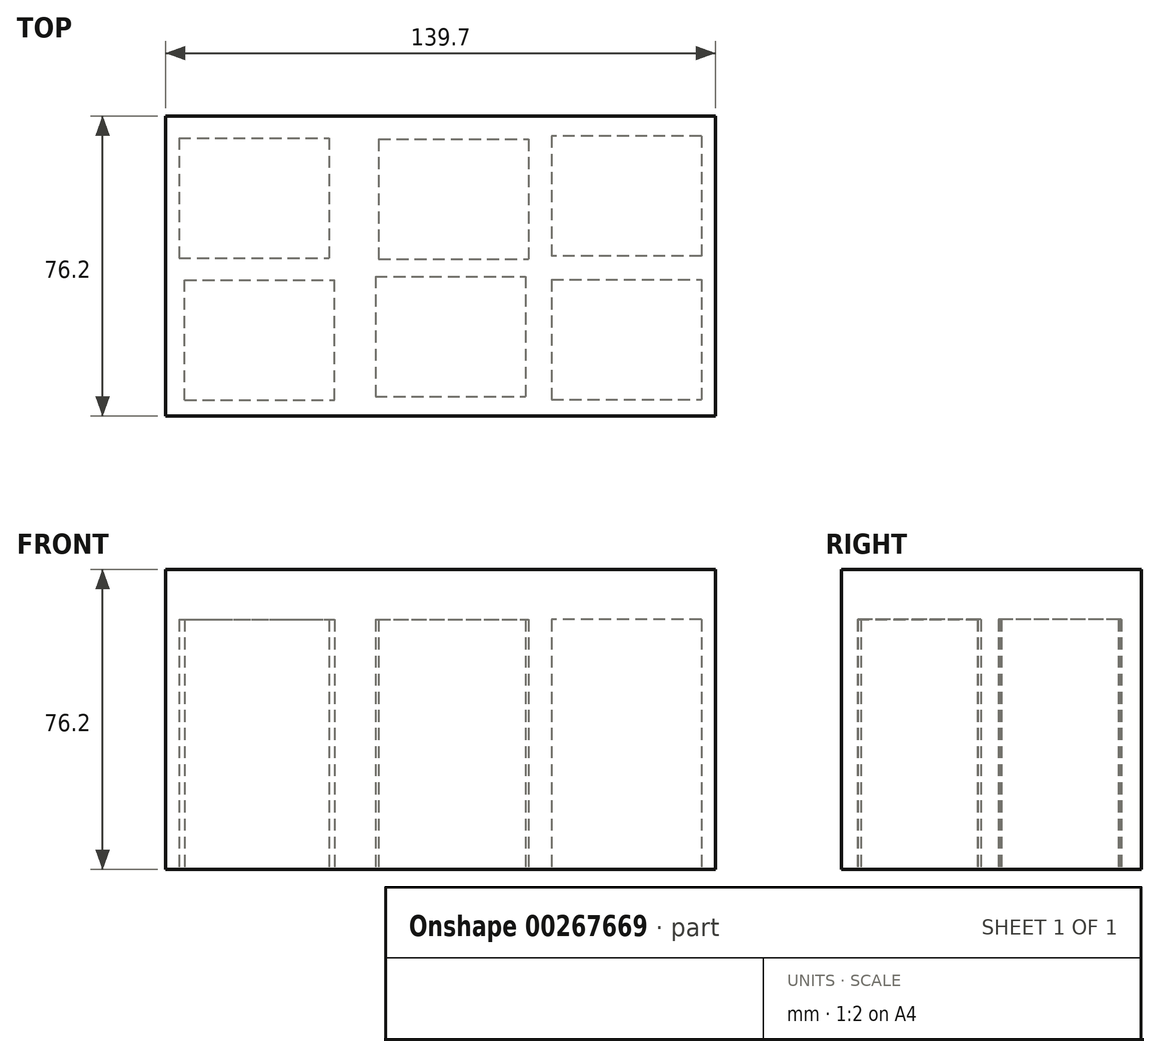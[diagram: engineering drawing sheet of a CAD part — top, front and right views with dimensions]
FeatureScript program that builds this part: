
annotation { "Feature Type Name" : "Feature", "Feature Type Description" : "" }
export const myFeature = defineFeature(function(context is Context, id is Id, definition is map)
    precondition{}
    {
        {
            var Q0;
            Q0=qCreatedBy(makeId("Top.planeOp"),FACE);
            var sketch = newSketch(context, id + "F0", { "sketchPlane" : qUnion([Q0])});
            skLineSegment(sketch, "E0.bottom", {"start": v(-69.85, -38.1) * mm, "end": v(69.85, -38.1) * mm});
            skLineSegment(sketch, "E0.top", {"start": v(-69.85, 38.1) * mm, "end": v(69.85, 38.1) * mm});
            skLineSegment(sketch, "E0.left", {"start": v(-69.85, -38.1) * mm, "end": v(-69.85, 38.1) * mm});
            skLineSegment(sketch, "E0.right", {"start": v(69.85, -38.1) * mm, "end": v(69.85, 38.1) * mm});
            skPoint(sketch, "E0.middle", {"position": v(0, 0) * mm});
            skLineSegment(sketch, "E1.bottom", {"start": v(-66.44, 32.56) * mm, "end": v(-28.34, 32.56) * mm});
            skLineSegment(sketch, "E1.top", {"start": v(-66.44, 2.08) * mm, "end": v(-28.34, 2.08) * mm});
            skLineSegment(sketch, "E1.left", {"start": v(-66.44, 32.56) * mm, "end": v(-66.44, 2.08) * mm});
            skLineSegment(sketch, "E1.right", {"start": v(-28.34, 32.56) * mm, "end": v(-28.34, 2.08) * mm});
            skLineSegment(sketch, "E2.bottom", {"start": v(-65.03, -34.1) * mm, "end": v(-26.93, -34.1) * mm});
            skLineSegment(sketch, "E2.top", {"start": v(-65.03, -3.61) * mm, "end": v(-26.93, -3.61) * mm});
            skLineSegment(sketch, "E2.left", {"start": v(-65.03, -34.1) * mm, "end": v(-65.03, -3.61) * mm});
            skLineSegment(sketch, "E2.right", {"start": v(-26.93, -34.1) * mm, "end": v(-26.93, -3.61) * mm});
            skLineSegment(sketch, "E3.bottom", {"start": v(-15.77, 32.25) * mm, "end": v(22.33, 32.25) * mm});
            skLineSegment(sketch, "E3.top", {"start": v(-15.77, 1.77) * mm, "end": v(22.33, 1.77) * mm});
            skLineSegment(sketch, "E3.left", {"start": v(-15.77, 32.25) * mm, "end": v(-15.77, 1.77) * mm});
            skLineSegment(sketch, "E3.right", {"start": v(22.33, 32.25) * mm, "end": v(22.33, 1.77) * mm});
            skLineSegment(sketch, "E4.bottom", {"start": v(66.28, 33.04) * mm, "end": v(28.18, 33.04) * mm});
            skLineSegment(sketch, "E4.top", {"start": v(66.28, 2.56) * mm, "end": v(28.18, 2.56) * mm});
            skLineSegment(sketch, "E4.left", {"start": v(66.28, 33.04) * mm, "end": v(66.28, 2.56) * mm});
            skLineSegment(sketch, "E4.right", {"start": v(28.18, 33.04) * mm, "end": v(28.18, 2.56) * mm});
            skLineSegment(sketch, "E5.bottom", {"start": v(-16.55, -2.63) * mm, "end": v(21.55, -2.63) * mm});
            skLineSegment(sketch, "E5.top", {"start": v(-16.55, -33.1) * mm, "end": v(21.55, -33.1) * mm});
            skLineSegment(sketch, "E5.left", {"start": v(-16.55, -2.63) * mm, "end": v(-16.55, -33.1) * mm});
            skLineSegment(sketch, "E5.right", {"start": v(21.55, -2.63) * mm, "end": v(21.55, -33.1) * mm});
            skLineSegment(sketch, "E6.bottom", {"start": v(28.18, -3.42) * mm, "end": v(66.28, -3.42) * mm});
            skLineSegment(sketch, "E6.top", {"start": v(28.18, -33.9) * mm, "end": v(66.28, -33.9) * mm});
            skLineSegment(sketch, "E6.left", {"start": v(28.18, -3.42) * mm, "end": v(28.18, -33.9) * mm});
            skLineSegment(sketch, "E6.right", {"start": v(66.28, -3.42) * mm, "end": v(66.28, -33.9) * mm});
            skSolve(sketch);
        }
        {
            var Q0;
            Q0=makeQuery(id+"F0.imprint","IMPRINT",FACE,{"disambiguationData":[TD([[makeQuery(id+"F0.imprint","IMPRINT",EDGE,{"derivedFrom":sQuery(id+"F0.wireOp",EDGE,"E0.bottom")}),1.0]])]});
            var Q1;
            Q1=makeQuery(id+"F0.imprint","IMPRINT",FACE,{"disambiguationData":[TD([[makeQuery(id+"F0.imprint","IMPRINT",EDGE,{"derivedFrom":sQuery(id+"F0.wireOp",EDGE,"E1.bottom")}),-1.0]])]});
            var Q2;
            Q2=makeQuery(id+"F0.imprint","IMPRINT",FACE,{"disambiguationData":[TD([[makeQuery(id+"F0.imprint","IMPRINT",EDGE,{"derivedFrom":sQuery(id+"F0.wireOp",EDGE,"E3.bottom")}),-1.0]])]});
            var Q3;
            Q3=makeQuery(id+"F0.imprint","IMPRINT",FACE,{"disambiguationData":[TD([[makeQuery(id+"F0.imprint","IMPRINT",EDGE,{"derivedFrom":sQuery(id+"F0.wireOp",EDGE,"E4.bottom")}),1.0]])]});
            var Q4;
            Q4=makeQuery(id+"F0.imprint","IMPRINT",FACE,{"disambiguationData":[TD([[makeQuery(id+"F0.imprint","IMPRINT",EDGE,{"derivedFrom":sQuery(id+"F0.wireOp",EDGE,"E6.bottom")}),-1.0]])]});
            var Q5;
            Q5=makeQuery(id+"F0.imprint","IMPRINT",FACE,{"disambiguationData":[TD([[makeQuery(id+"F0.imprint","IMPRINT",EDGE,{"derivedFrom":sQuery(id+"F0.wireOp",EDGE,"E5.bottom")}),-1.0]])]});
            var Q6;
            Q6=makeQuery(id+"F0.imprint","IMPRINT",FACE,{"disambiguationData":[TD([[makeQuery(id+"F0.imprint","IMPRINT",EDGE,{"derivedFrom":sQuery(id+"F0.wireOp",EDGE,"E2.bottom")}),1.0]])]});
            extrude(context, id + "F1", {"entities" : qUnion([Q0, Q1, Q2, Q3, Q4, Q5, Q6]), "depth" : 76.2 * mm});
        }
        {
            var Q0;
            Q0=makeQuery(id+"F0.imprint","IMPRINT",FACE,{"disambiguationData":[TD([[makeQuery(id+"F0.imprint","IMPRINT",EDGE,{"derivedFrom":sQuery(id+"F0.wireOp",EDGE,"E1.bottom")}),-1.0]])]});
            var Q1;
            Q1=makeQuery(id+"F0.imprint","IMPRINT",FACE,{"disambiguationData":[TD([[makeQuery(id+"F0.imprint","IMPRINT",EDGE,{"derivedFrom":sQuery(id+"F0.wireOp",EDGE,"E3.bottom")}),-1.0]])]});
            var Q2;
            Q2=makeQuery(id+"F0.imprint","IMPRINT",FACE,{"disambiguationData":[TD([[makeQuery(id+"F0.imprint","IMPRINT",EDGE,{"derivedFrom":sQuery(id+"F0.wireOp",EDGE,"E4.bottom")}),1.0]])]});
            var Q3;
            Q3=makeQuery(id+"F0.imprint","IMPRINT",FACE,{"disambiguationData":[TD([[makeQuery(id+"F0.imprint","IMPRINT",EDGE,{"derivedFrom":sQuery(id+"F0.wireOp",EDGE,"E6.bottom")}),-1.0]])]});
            var Q4;
            Q4=makeQuery(id+"F0.imprint","IMPRINT",FACE,{"disambiguationData":[TD([[makeQuery(id+"F0.imprint","IMPRINT",EDGE,{"derivedFrom":sQuery(id+"F0.wireOp",EDGE,"E5.bottom")}),-1.0]])]});
            var Q5;
            Q5=makeQuery(id+"F0.imprint","IMPRINT",FACE,{"disambiguationData":[TD([[makeQuery(id+"F0.imprint","IMPRINT",EDGE,{"derivedFrom":sQuery(id+"F0.wireOp",EDGE,"E2.bottom")}),1.0]])]});
            extrude(context, id + "F2", {"entities" : qUnion([Q0, Q1, Q2, Q3, Q4, Q5]), "operationType" : NewBodyOperationType.REMOVE, "depth" : 63.5 * mm});
        }
    });
